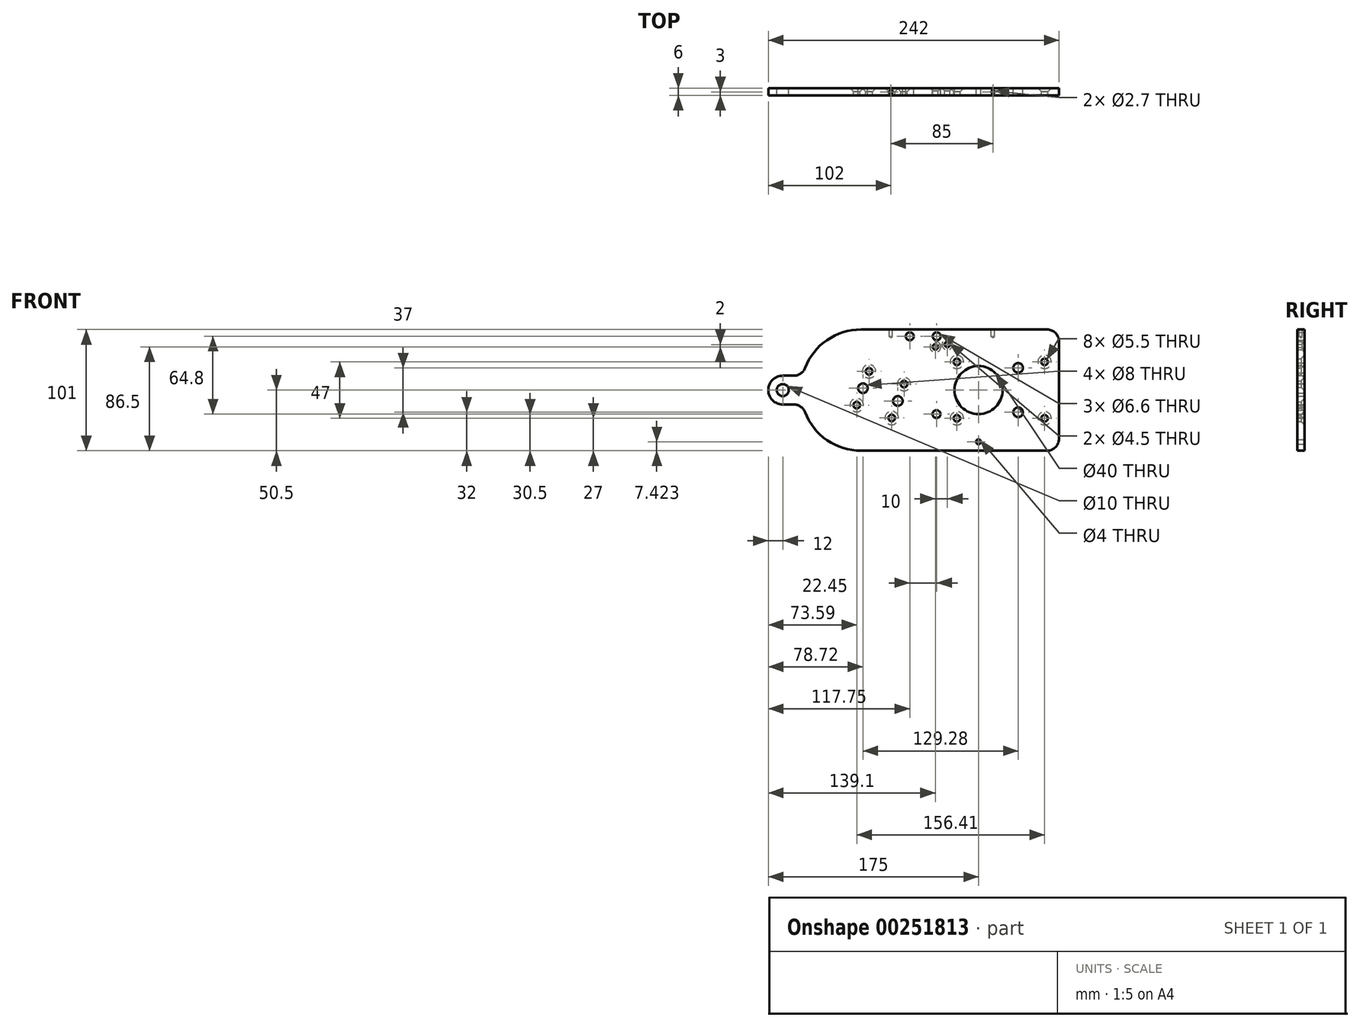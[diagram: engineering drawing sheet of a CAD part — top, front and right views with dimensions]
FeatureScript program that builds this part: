
annotation { "Feature Type Name" : "Feature", "Feature Type Description" : "" }
export const myFeature = defineFeature(function(context is Context, id is Id, definition is map)
    precondition{}
    {
        {
            var Q0;
            Q0=qCreatedBy(makeId("Front.planeOp"),FACE);
            var sketch = newSketch(context, id + "F0", { "sketchPlane" : qUnion([Q0])});
            skLineSegment(sketch, "E0", {"start": v(-253.43, 0) * mm, "end": v(124.03, 0) * mm, "construction": true});
            skLineSegment(sketch, "E1", {"start": v(-97.78, -50.5) * mm, "end": v(57, -50.5) * mm});
            skLineSegment(sketch, "E2", {"start": v(67, -40.5) * mm, "end": v(67, 40.5) * mm});
            skLineSegment(sketch, "E3", {"start": v(57, 50.5) * mm, "end": v(-97.78, 50.5) * mm});
            skCircle(sketch, "E4", {"center": v(0, 0) * mm, "radius": 20 * mm});
            skArc(sketch, "E5", {"start": v(-163, 12) * mm, "mid": v(-175, 0) * mm, "end": v(-163, -12) * mm});
            skCircle(sketch, "E6", {"center": v(-163, 0) * mm, "radius": 5 * mm});
            skLineSegment(sketch, "E7", {"start": v(-163, 44.7) * mm, "end": v(-163, -57.27) * mm, "construction": true});
            skLineSegment(sketch, "E8", {"start": v(-163, 12) * mm, "end": v(-153.8, 12) * mm});
            skLineSegment(sketch, "E9", {"start": v(-163, -12) * mm, "end": v(-153.8, -12) * mm});
            skArc(sketch, "E10", {"start": v(-97.78, 50.5) * mm, "mid": v(-126.1, 41.7) * mm, "end": v(-144.46, 18.42) * mm});
            skArc(sketch, "E11", {"start": v(-153.8, 12) * mm, "mid": v(-148.14, 13.76) * mm, "end": v(-144.46, 18.42) * mm});
            skArc(sketch, "E12.MirrorCS", {"start": v(-97.78, -50.5) * mm, "mid": v(-126.1, -41.7) * mm, "end": v(-144.46, -18.42) * mm});
            skArc(sketch, "E13.MirrorCS", {"start": v(-153.8, -12) * mm, "mid": v(-148.14, -13.76) * mm, "end": v(-144.46, -18.42) * mm});
            skPoint(sketch, "E14.visualSharp", {"position": v(67, 50.5) * mm});
            skArc(sketch, "E14.filletArc", {"start": v(67, 40.5) * mm, "mid": v(64.07, 47.57) * mm, "end": v(57, 50.5) * mm});
            skPoint(sketch, "E15.visualSharp", {"position": v(67, -50.5) * mm});
            skArc(sketch, "E15.filletArc", {"start": v(57, -50.5) * mm, "mid": v(64.07, -47.57) * mm, "end": v(67, -40.5) * mm});
            skLineSegment(sketch, "E16", {"start": v(-35.13, 23.5) * mm, "end": v(54.06, 23.5) * mm, "construction": true});
            skLineSegment(sketch, "E17", {"start": v(-36.86, -23.5) * mm, "end": v(56.13, -23.5) * mm, "construction": true});
            skLineSegment(sketch, "E18", {"start": v(-62.98, 44.8) * mm, "end": v(-33.6, 44.8) * mm, "construction": true});
            skLineSegment(sketch, "E19", {"start": v(55, 45.35) * mm, "end": v(55, -35.65) * mm, "construction": true});
            skPoint(sketch, "E20", {"position": v(55, 23.5) * mm});
            skPoint(sketch, "E21", {"position": v(55, -23.5) * mm});
            skLineSegment(sketch, "E22", {"start": v(-18, 40.78) * mm, "end": v(-18, -32.6) * mm, "construction": true});
            skPoint(sketch, "E23", {"position": v(-18, -23.5) * mm});
            skPoint(sketch, "E24", {"position": v(-18, 23.5) * mm});
            skPoint(sketch, "E25", {"position": v(-57.25, 44.8) * mm});
            skPoint(sketch, "E26", {"position": v(-34.8, 44.8) * mm});
            skLineSegment(sketch, "E27", {"start": v(33, 25.48) * mm, "end": v(33, -36.21) * mm, "construction": true});
            skPoint(sketch, "E28", {"position": v(33, 18.5) * mm});
            skPoint(sketch, "E29", {"position": v(33, -18.5) * mm});
            skLineSegment(sketch, "E30", {"start": v(0, 72.66) * mm, "end": v(0, -73.2) * mm, "construction": true});
            skPoint(sketch, "E31", {"position": v(-25.9, 38) * mm});
            skPoint(sketch, "E32", {"position": v(-35.9, 36) * mm});
            skPoint(sketch, "E33", {"position": v(0, -43.08) * mm});
            skPoint(sketch, "E34", {"position": v(0, -42.9) * mm});
            skPoint(sketch, "E35", {"position": v(-35, -20) * mm});
            skPoint(sketch, "E36", {"position": v(-62.02, 5) * mm});
            skPoint(sketch, "E37", {"position": v(-67.15, -9.1) * mm});
            skPoint(sketch, "E38", {"position": v(-72.28, -23.2) * mm});
            skPoint(sketch, "E39", {"position": v(-91.15, 15.6) * mm});
            skPoint(sketch, "E40", {"position": v(-96.28, 1.52) * mm});
            skPoint(sketch, "E41", {"position": v(-101.4, -12.56) * mm});
            skSolve(sketch);
        }
        {
            var Q0;
            Q0=makeQuery(id+"F0.imprint","IMPRINT",FACE,{"disambiguationData":[TD([[makeQuery(id+"F0.imprint","IMPRINT",EDGE,{"derivedFrom":sQuery(id+"F0.wireOp",EDGE,"E1")}),1.0]])]});
            extrude(context, id + "F1", {"entities" : qUnion([Q0]), "depth" : 6 * mm});
        }
        {
            var Q0;
            Q0=sQuery(id+"F0.wireOp",VERTEX,"E20");
            var Q1;
            Q1=sQuery(id+"F0.wireOp",VERTEX,"E21");
            var Q2;
            Q2=sQuery(id+"F0.wireOp",VERTEX,"E24");
            var Q3;
            Q3=sQuery(id+"F0.wireOp",VERTEX,"E23");
            var Q4;
            Q4=sQuery(id+"F0.wireOp",VERTEX,"E36");
            var Q5;
            Q5=sQuery(id+"F0.wireOp",VERTEX,"E38");
            var Q6;
            Q6=sQuery(id+"F0.wireOp",VERTEX,"E39");
            var Q7;
            Q7=sQuery(id+"F0.wireOp",VERTEX,"E41");
            var Q8;
            Q8=makeQuery(id+"F1.opExtrude","SWEPT_BODY",BODY,{"disambiguationData":[OSD([sQuery(id+"F0.wireOp",EDGE,"E1"),sQuery(id+"F0.wireOp",EDGE,"E2"),sQuery(id+"F0.wireOp",EDGE,"E3"),sQuery(id+"F0.wireOp",EDGE,"E4"),sQuery(id+"F0.wireOp",EDGE,"E5"),sQuery(id+"F0.wireOp",EDGE,"E6"),sQuery(id+"F0.wireOp",EDGE,"E8"),sQuery(id+"F0.wireOp",EDGE,"E9"),sQuery(id+"F0.wireOp",EDGE,"E10"),sQuery(id+"F0.wireOp",EDGE,"E11"),sQuery(id+"F0.wireOp",EDGE,"E12.MirrorCS"),sQuery(id+"F0.wireOp",EDGE,"E13.MirrorCS"),sQuery(id+"F0.wireOp",EDGE,"E14.filletArc"),sQuery(id+"F0.wireOp",EDGE,"E15.filletArc")])]});
            hole(context, id + "F2", {"style" : HoleStyle.C_SINK, "endStyle" : HoleEndStyle.THROUGH, "oppositeDirection" : true, "standardTappedOrClearance" : lookupTablePath({ "standard" : "ISO", "fit" : "Normal", "size" : "M5", "type" : "Clearance" }), "standardBlindInLast" : lookupTablePath({ "fit" : "Standard", "standard" : "ISO", "size" : "M5", "type" : "Clearance" }), "holeDiameter" : 5.5 * mm, "cSinkDiameter" : 11.2 * mm, "cSinkAngle" : 90 * degree, "tappedDepth" : 12 * mm, "tapClearance" : 3, "locations" : qUnion([Q0, Q1, Q2, Q3, Q4, Q5, Q6, Q7]), "scope" : qUnion([Q8])});
        }
        {
            var Q0;
            Q0=sQuery(id+"F0.wireOp",VERTEX,"E25");
            var Q1;
            Q1=sQuery(id+"F0.wireOp",VERTEX,"E26");
            var Q2;
            Q2=sQuery(id+"F0.wireOp",VERTEX,"E35");
            var Q3;
            Q3=makeQuery(id+"F1.opExtrude","SWEPT_BODY",BODY,{"disambiguationData":[OSD([sQuery(id+"F0.wireOp",EDGE,"E1"),sQuery(id+"F0.wireOp",EDGE,"E2"),sQuery(id+"F0.wireOp",EDGE,"E3"),sQuery(id+"F0.wireOp",EDGE,"E4"),sQuery(id+"F0.wireOp",EDGE,"E5"),sQuery(id+"F0.wireOp",EDGE,"E6"),sQuery(id+"F0.wireOp",EDGE,"E8"),sQuery(id+"F0.wireOp",EDGE,"E9"),sQuery(id+"F0.wireOp",EDGE,"E10"),sQuery(id+"F0.wireOp",EDGE,"E11"),sQuery(id+"F0.wireOp",EDGE,"E12.MirrorCS"),sQuery(id+"F0.wireOp",EDGE,"E13.MirrorCS"),sQuery(id+"F0.wireOp",EDGE,"E14.filletArc"),sQuery(id+"F0.wireOp",EDGE,"E15.filletArc")])]});
            hole(context, id + "F3", {"style" : HoleStyle.SIMPLE, "endStyle" : HoleEndStyle.THROUGH, "oppositeDirection" : true, "standardTappedOrClearance" : lookupTablePath({ "standard" : "ISO", "fit" : "Normal", "size" : "M6", "type" : "Clearance" }), "standardBlindInLast" : lookupTablePath({ "fit" : "Standard", "standard" : "ISO", "size" : "M6", "type" : "Clearance" }), "holeDiameter" : 6.6 * mm, "tappedDepth" : 12 * mm, "tapClearance" : 3, "locations" : qUnion([Q0, Q1, Q2]), "scope" : qUnion([Q3])});
        }
        {
            var Q0;
            Q0=sQuery(id+"F0.wireOp",VERTEX,"E32");
            var Q1;
            Q1=sQuery(id+"F0.wireOp",VERTEX,"E31");
            var Q2;
            Q2=makeQuery(id+"F1.opExtrude","SWEPT_BODY",BODY,{"disambiguationData":[OSD([sQuery(id+"F0.wireOp",EDGE,"E1"),sQuery(id+"F0.wireOp",EDGE,"E2"),sQuery(id+"F0.wireOp",EDGE,"E3"),sQuery(id+"F0.wireOp",EDGE,"E4"),sQuery(id+"F0.wireOp",EDGE,"E5"),sQuery(id+"F0.wireOp",EDGE,"E6"),sQuery(id+"F0.wireOp",EDGE,"E8"),sQuery(id+"F0.wireOp",EDGE,"E9"),sQuery(id+"F0.wireOp",EDGE,"E10"),sQuery(id+"F0.wireOp",EDGE,"E11"),sQuery(id+"F0.wireOp",EDGE,"E12.MirrorCS"),sQuery(id+"F0.wireOp",EDGE,"E13.MirrorCS"),sQuery(id+"F0.wireOp",EDGE,"E14.filletArc"),sQuery(id+"F0.wireOp",EDGE,"E15.filletArc")])]});
            hole(context, id + "F4", {"style" : HoleStyle.C_SINK, "endStyle" : HoleEndStyle.THROUGH, "oppositeDirection" : true, "holeDiameter" : 4.5 * mm, "cSinkDiameter" : 8.96 * mm, "cSinkAngle" : 90 * degree, "tappedDepth" : 12 * mm, "tapClearance" : 3, "locations" : qUnion([Q0, Q1]), "scope" : qUnion([Q2])});
        }
        {
            var Q0;
            Q0=sQuery(id+"F0.wireOp",VERTEX,"E33");
            var Q1;
            Q1=makeQuery(id+"F1.opExtrude","SWEPT_BODY",BODY,{"disambiguationData":[OSD([sQuery(id+"F0.wireOp",EDGE,"E1"),sQuery(id+"F0.wireOp",EDGE,"E2"),sQuery(id+"F0.wireOp",EDGE,"E3"),sQuery(id+"F0.wireOp",EDGE,"E4"),sQuery(id+"F0.wireOp",EDGE,"E5"),sQuery(id+"F0.wireOp",EDGE,"E6"),sQuery(id+"F0.wireOp",EDGE,"E8"),sQuery(id+"F0.wireOp",EDGE,"E9"),sQuery(id+"F0.wireOp",EDGE,"E10"),sQuery(id+"F0.wireOp",EDGE,"E11"),sQuery(id+"F0.wireOp",EDGE,"E12.MirrorCS"),sQuery(id+"F0.wireOp",EDGE,"E13.MirrorCS"),sQuery(id+"F0.wireOp",EDGE,"E14.filletArc"),sQuery(id+"F0.wireOp",EDGE,"E15.filletArc")])]});
            hole(context, id + "F5", {"style" : HoleStyle.SIMPLE, "endStyle" : HoleEndStyle.THROUGH, "oppositeDirection" : true, "holeDiameter" : 4 * mm, "tappedDepth" : 12 * mm, "tapClearance" : 3, "locations" : qUnion([Q0]), "scope" : qUnion([Q1])});
        }
        {
            var Q0;
            Q0=sQuery(id+"F0.wireOp",VERTEX,"E28");
            var Q1;
            Q1=sQuery(id+"F0.wireOp",VERTEX,"E29");
            var Q2;
            Q2=sQuery(id+"F0.wireOp",VERTEX,"E37");
            var Q3;
            Q3=sQuery(id+"F0.wireOp",VERTEX,"E40");
            var Q4;
            Q4=makeQuery(id+"F1.opExtrude","SWEPT_BODY",BODY,{"disambiguationData":[OSD([sQuery(id+"F0.wireOp",EDGE,"E1"),sQuery(id+"F0.wireOp",EDGE,"E2"),sQuery(id+"F0.wireOp",EDGE,"E3"),sQuery(id+"F0.wireOp",EDGE,"E4"),sQuery(id+"F0.wireOp",EDGE,"E5"),sQuery(id+"F0.wireOp",EDGE,"E6"),sQuery(id+"F0.wireOp",EDGE,"E8"),sQuery(id+"F0.wireOp",EDGE,"E9"),sQuery(id+"F0.wireOp",EDGE,"E10"),sQuery(id+"F0.wireOp",EDGE,"E11"),sQuery(id+"F0.wireOp",EDGE,"E12.MirrorCS"),sQuery(id+"F0.wireOp",EDGE,"E13.MirrorCS"),sQuery(id+"F0.wireOp",EDGE,"E14.filletArc"),sQuery(id+"F0.wireOp",EDGE,"E15.filletArc")])]});
            hole(context, id + "F6", {"style" : HoleStyle.SIMPLE, "endStyle" : HoleEndStyle.THROUGH, "oppositeDirection" : true, "holeDiameter" : 8 * mm, "tappedDepth" : 12 * mm, "tapClearance" : 3, "locations" : qUnion([Q0, Q1, Q2, Q3]), "scope" : qUnion([Q4])});
        }
        {
            var Q0;
            Q0=makeQuery(id+"F1.opExtrude","SWEPT_FACE",FACE,{"disambiguationData":[OSD([sQuery(id+"F0.wireOp",EDGE,"E3")])]});
            var sketch = newSketch(context, id + "F7", { "sketchPlane" : qUnion([Q0])});
            skLineSegment(sketch, "E42", {"start": v(-215.82, -3) * mm, "end": v(123.22, -3) * mm, "construction": true});
            skPoint(sketch, "E43", {"position": v(12, -3) * mm});
            skPoint(sketch, "E44", {"position": v(-73, -3) * mm});
            skPoint(sketch, "E45.MirrorP", {"position": v(-73, 3) * mm});
            skPoint(sketch, "E46.MirrorP", {"position": v(12, 3) * mm});
            skSolve(sketch);
        }
        {
            var Q0;
            Q0=sQuery(id+"F7.wireOp",VERTEX,"E44");
            var Q1;
            Q1=sQuery(id+"F7.wireOp",VERTEX,"E43");
            var Q2;
            Q2=makeQuery(id+"F1.opExtrude","SWEPT_BODY",BODY,{"disambiguationData":[OSD([sQuery(id+"F0.wireOp",EDGE,"E1"),sQuery(id+"F0.wireOp",EDGE,"E2"),sQuery(id+"F0.wireOp",EDGE,"E3"),sQuery(id+"F0.wireOp",EDGE,"E4"),sQuery(id+"F0.wireOp",EDGE,"E5"),sQuery(id+"F0.wireOp",EDGE,"E6"),sQuery(id+"F0.wireOp",EDGE,"E8"),sQuery(id+"F0.wireOp",EDGE,"E9"),sQuery(id+"F0.wireOp",EDGE,"E10"),sQuery(id+"F0.wireOp",EDGE,"E11"),sQuery(id+"F0.wireOp",EDGE,"E12.MirrorCS"),sQuery(id+"F0.wireOp",EDGE,"E13.MirrorCS"),sQuery(id+"F0.wireOp",EDGE,"E14.filletArc"),sQuery(id+"F0.wireOp",EDGE,"E15.filletArc")])]});
            hole(context, id + "F8", {"style" : HoleStyle.SIMPLE, "endStyle" : HoleEndStyle.BLIND, "holeDiameter" : 2.7 * mm, "holeDepth" : 6 * mm, "tappedDepth" : 12 * mm, "tapClearance" : 3, "locations" : qUnion([Q0, Q1]), "scope" : qUnion([Q2])});
        }
    });
